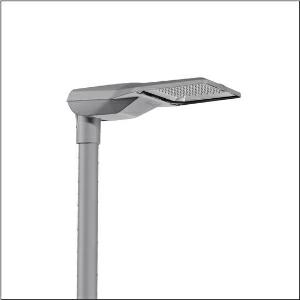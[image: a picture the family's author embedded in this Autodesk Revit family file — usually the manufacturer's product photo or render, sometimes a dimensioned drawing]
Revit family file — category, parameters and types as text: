
# Revit family: streetlight_sl_21_midi___stw1_0a_5xe7e33a08lb_1090
name_source: partatom
category: Lighting Fixtures
units: mm (PartAtom-declared; Revit-internal decimal feet)

## family parameters
Cut with Voids When Loaded = No
Host = Face
Light Source = No
Part Type = Normal
Room Calculation Point = No
Round Connector Dimension = Use Diameter
Shared = No

## types (1)
- --- (1 x LED, 14340 lm, 98.3 W, 3000K)
    Apparent Load = 98 VA
    CIE Flux Codes = 38 75 98 100 100
    Color Rendering = 70
    Color Temperature = 3000K
    Default Elevation = 1800 mm
    Description = Streetlight SL 21 midi, mast luminaire, primary light control with lens, of PMMA, primary optical cover: cover, of toughened safety glass, transparent, light distribution: STW1.0a, light emission: direct distribution, primary light characteristic: asymmetric, installation type: post-top, side-entry, LED, 3G 1.5mm², High Power LED, rated luminous flux: 14.340lm, luminous efficacy: 146lm/W, light colour: 730, colour temperature: 3000K, control: overheat protection, constant luminous flux control, time-dependent luminous flux control, flexible luminous flux parameterisation, mains connection: 220..240V, AC, 50/60Hz, connection cable pre-assembled, cable length: 10,5m, wiring characteristics: H07RN-F, start of lifetime: 98W, end of service life: 101W, reduction: 44W, luminaire housing, of diecast aluminium, powder-coated, Siteco® metallic grey (DB 702S), corrosivity category C5 mid according to DIN EN ISO 12944, please order mast flange separately, inclination adjustable: 0°, 5°, 10°, 15°, sealing non-destructively replaceable, multi-level sealing system, length: 644mm, width: 335mm, height: 110mm, mast flange for spigot size: 42mm (side-entry): 5XC10008XM4, 60/48mm (side-entry/post-top): 5XC10108XM2, 76/60mm (side-entry/post-top): 5XC10108XM1, protection rating (complete): IP66, insulation class (complete): insulation class II (safety insulation), certification: CE, ENEC, ENEC+, VDE, impact resistance: IK09, permissible operating ambient temperature for outdoor applications: -40..+50°C, standard-compliant lighting for roads and squares, packaging unit: 1 piece

Light Distribution: STW1.0a
    Height = 111 mm
    Lamp = 1 x LED
    Lamp Light Flux = 14340 lm
    Lamp Power = 98.3 W
    Lamp count = 1
    Length = 644 mm
    Luminous efficacy = 146 lm/W
    Manufacturer = Siteco
    ModVariant = No
    Model = 5XE7E33A08LB
    Number of Poles = 1
    OnlyDefault = Yes
    Power Factor = 1
    Product Name = Streetlight SL 21 midi | STW1.0a
    Product group = mast luminaire | pylon top
    ProductGroupID = 6100
    Protection Class = Protection class II
    Protection Degree = IP 66
    RLX_Detail_Level = 1
    RLX_Emergency_Light_Flux = 0 lm
    RLX_Emergency_Type = 0
    RLX_Emergency_Type_DB = No
    RlxData = <blob elided: 90221 chars, md5=7b424657>
    Socket = socket
    Standby Power = 0 W
    System Light Flux = 14340 lm
    System Power = 98 W
    Type Comments = factory setting: luminous flux: 100 % | Output Level: 100 % | 1020 mA
    Type Image = l_1004298.jpg
    URL = http://relux.com
    VarID = @adj_139621
    Voltage = 0 V
    Weight = 0.00 kg
    Width = 336 mm

## geometry (parser evidence)
native form markers: Blend x4, Sweep x11
no freeform markers — native parametric forms only
